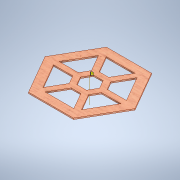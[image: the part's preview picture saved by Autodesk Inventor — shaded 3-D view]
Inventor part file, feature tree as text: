
AUTODESK INVENTOR PART (.ipt)
format: ipt  version: 2020 (Build 240168000, 168)  size: 284,160 bytes
history: native  units: mm
features: sketch x2, extrude x2
ambient origin geometry x8: Origin, YZ Plane, XZ Plane, XY Plane, X Axis, Y Axis, Z Axis, Center Point
bodies: Body1 (feature_tree)
feature tree (4):
  sketch  "Sketch6"  dims[d72=6.5mm d85=2.0mm d86=0.0mm]
  extrude  "Fronte"  Depth=2.0mm TaperAngle=0.0deg
  extrude  "Extrusion17"  Depth=2.0mm
  sketch  "Sketch11"  dims[d87=15.0mm d88=6.5mm d91=2.5mm d92=2.5mm d95=1.25mm d96=25.0mm d97=2.5mm d98=25.0mm d99=135.0deg d100=0.0mm d114=1.7mm d117=3.0mm d121=3.0mm d123=6.0mm d127=140.0mm d128=5.196152mm d129=5.196152mm d130=3.0mm d158=110.0mm d159=50.0mm d160=30.0mm d162=60.0mm d164=360.0deg d166=2.0mm d167=0.0mm]
